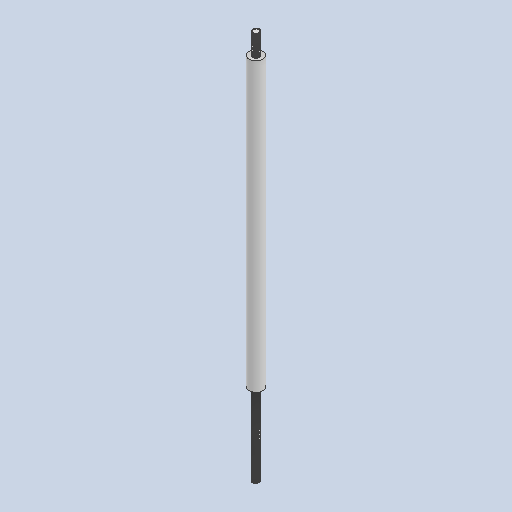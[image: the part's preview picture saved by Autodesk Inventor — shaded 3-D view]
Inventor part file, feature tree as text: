
AUTODESK INVENTOR PART (.ipt)
format: ipt  version: 2024.2 (Build 282272000, 272)  size: 3,062,784 bytes
history: native  units: mm
features: sketch x4, revolve x3, other x1, thread x1, helix x1
ambient origin geometry x8: Origin, YZ Plane, XZ Plane, XY Plane, X Axis, Y Axis, Z Axis, Center Point
bodies: Solid2 (feature_tree)
feature tree (10):
  other  "Sólido1"
  revolve  "Revolución1"  [1 undecoded]
  thread  "Rosca1"  [1 undecoded]
  revolve  "Revolution2"  Angle=90.0deg
  revolve  "Revolution3"  [1 undecoded]
  helix  "Coil1"  [1 undecoded]
  sketch  "Boceto1"  dims[d1=3.0mm d2=6.0mm d3=9.0mm]
  sketch  "Sketch2"  dims[d4=123.0mm d5=90.0deg]
  sketch  "Sketch3"  dims[d6=144.0mm d7=0.0mm d8=35.0mm]
  sketch  "Sketch4"  dims[d9=0.108253mm d10=0.0625mm d11=0.03125mm d12=0.054127mm d13=0.5mm d15=60.0deg d18=0.0625mm d20=60.0deg d21=0.0mm d22=0.0mm d23=0.5005mm d24=168.0mm d25=10.0mm d26=0.0mm d27=0.0mm d28=0.0mm d29=0.0mm d30=0.0mm]
note: 4 required parameter values undecoded (feature->parameter linkage not recoverable at this tier; creation-order binding heuristic only, values carry confidence <= 0.55)